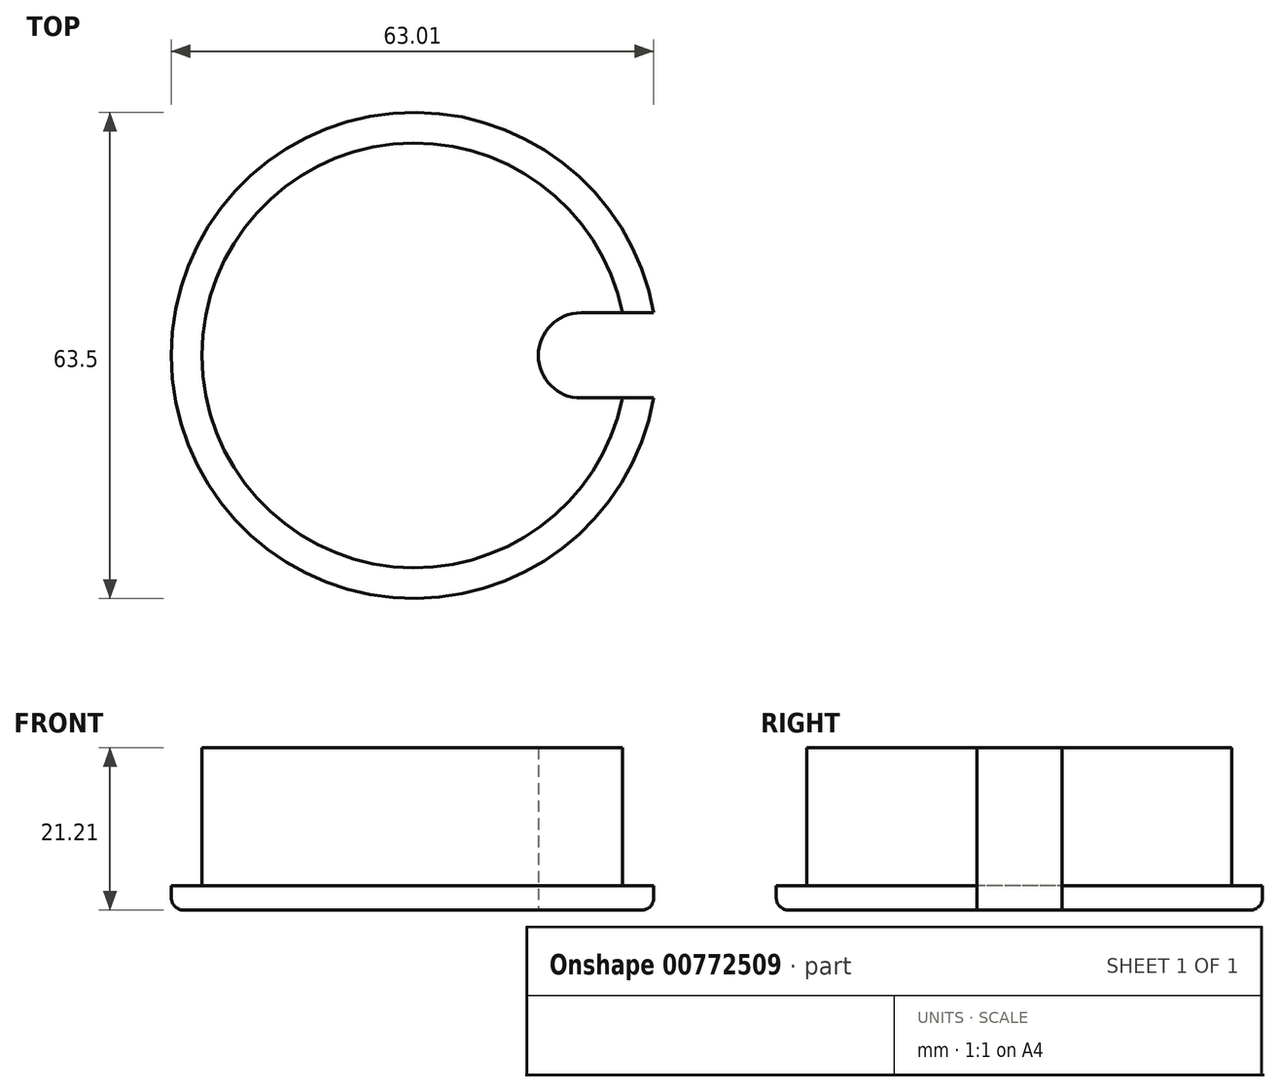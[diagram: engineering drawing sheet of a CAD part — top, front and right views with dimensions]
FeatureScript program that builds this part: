
annotation { "Feature Type Name" : "Feature", "Feature Type Description" : "" }
export const myFeature = defineFeature(function(context is Context, id is Id, definition is map)
    precondition{}
    {
        {
            var Q0;
            Q0=qCreatedBy(makeId("Top.planeOp"),FACE);
            var sketch = newSketch(context, id + "F0", { "sketchPlane" : qUnion([Q0])});
            skCircle(sketch, "E0", {"center": v(0, 0) * mm, "radius": 31.75 * mm});
            skSolve(sketch);
        }
        {
            var Q0;
            Q0 = qSketchRegion(id + "F0", true);
            extrude(context, id + "F1", {"entities" : qUnion([Q0]), "depth" : 3.17 * mm, "offsetDistance" : 25.4 * mm});
        }
        {
            var Q0;
            Q0=makeQuery(id+"F1.opExtrude","CAP_FACE",FACE,{"disambiguationData":[OSD([sQuery(id+"F0.wireOp",EDGE,"E0")])],"isStart":false});
            var sketch = newSketch(context, id + "F2", { "sketchPlane" : qUnion([Q0])});
            skCircle(sketch, "E1", {"center": v(0, 0) * mm, "radius": 27.75 * mm});
            skSolve(sketch);
        }
        {
            var Q0;
            Q0 = qSketchRegion(id + "F2", true);
            extrude(context, id + "F3", {"entities" : qUnion([Q0]), "operationType" : NewBodyOperationType.ADD, "depth" : 18.03 * mm, "offsetDistance" : 25.4 * mm});
        }
        {
            var Q0;
            Q0=makeQuery(id+"F1.opExtrude","CAP_FACE",FACE,{"disambiguationData":[OSD([sQuery(id+"F0.wireOp",EDGE,"E0")])],"isStart":true});
            var sketch = newSketch(context, id + "F4", { "sketchPlane" : qUnion([Q0])});
            skLineSegment(sketch, "E2", {"start": v(31.27, 5.56) * mm, "end": v(21.74, 5.56) * mm});
            skArc(sketch, "E3", {"start": v(21.74, 5.56) * mm, "mid": v(16.19, 0) * mm, "end": v(21.74, -5.56) * mm});
            skLineSegment(sketch, "E4", {"start": v(21.74, -5.56) * mm, "end": v(31.27, -5.56) * mm});
            skSolve(sketch);
        }
        {
            var Q0;
            {var subQ0=sQuery(id+"F4.wireOp",EDGE,"E3");Q0=makeQuery(id+"F4.imprint","IMPRINT",FACE,{"disambiguationData":[TD([[makeQuery(id+"F4.imprint","IMPRINT",EDGE,{"derivedFrom":subQ0}),1.0]])]});}
            extrude(context, id + "F5", {"entities" : qUnion([Q0]), "operationType" : NewBodyOperationType.REMOVE, "oppositeDirection" : true, "depth" : 25.4 * mm, "offsetDistance" : 25.4 * mm});
        }
        {
            var Q0;
            Q0=makeQuery(id+"F1.opExtrude","CAP_EDGE",EDGE,{"disambiguationData":[OSD([sQuery(id+"F0.wireOp",EDGE,"E0")])],"isStart":true});
            var Q1;
            Q1=makeQuery(id+"F5.boolean.opBoolean","COPY",EDGE,{"derivedFrom":makeQuery(id+"F5.opExtrude","CAP_EDGE",EDGE,{"disambiguationData":[OSD([sQuery(id+"F4.wireOp",EDGE,"E2")])],"isStart":true})});
            var Q2;
            Q2=makeQuery(id+"F5.boolean.opBoolean","COPY",EDGE,{"derivedFrom":makeQuery(id+"F5.opExtrude","CAP_EDGE",EDGE,{"disambiguationData":[OSD([sQuery(id+"F4.wireOp",EDGE,"E3")])],"isStart":true})});
            var Q3;
            Q3=makeQuery(id+"F5.boolean.opBoolean","COPY",EDGE,{"derivedFrom":makeQuery(id+"F5.opExtrude","CAP_EDGE",EDGE,{"disambiguationData":[OSD([sQuery(id+"F4.wireOp",EDGE,"E4")])],"isStart":true})});
            fillet(context, id + "F6", {"entities" : qUnion([Q0, Q1, Q2, Q3]), "radius" : 1.59 * mm, "tangentPropagation" : true, "allowEdgeOverflow" : false});
        }
    });
